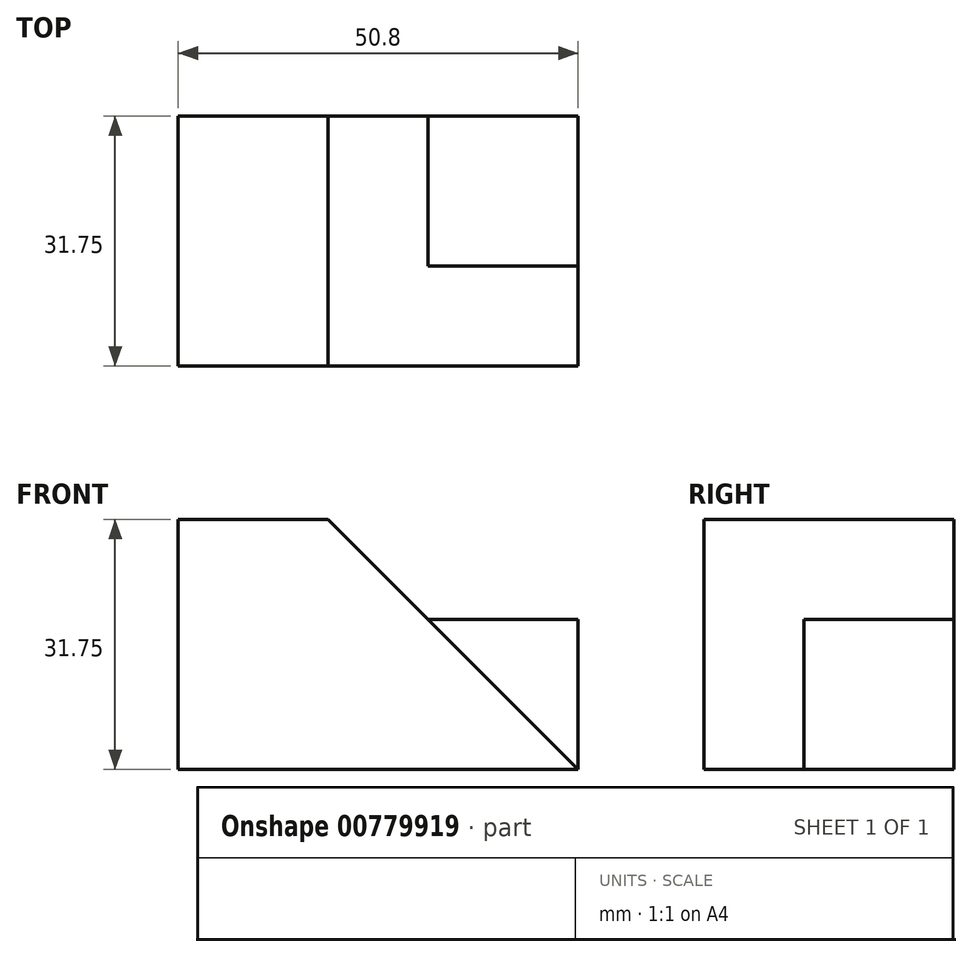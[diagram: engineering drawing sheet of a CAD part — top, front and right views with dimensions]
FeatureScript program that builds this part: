
annotation { "Feature Type Name" : "Feature", "Feature Type Description" : "" }
export const myFeature = defineFeature(function(context is Context, id is Id, definition is map)
    precondition{}
    {
        {
            var Q0;
            Q0=qCreatedBy(makeId("Front.planeOp"),FACE);
            var sketch = newSketch(context, id + "F0", { "sketchPlane" : qUnion([Q0])});
            skLineSegment(sketch, "E0", {"start": v(0, 0) * mm, "end": v(0, 31.75) * mm});
            skLineSegment(sketch, "E1", {"start": v(0, 31.75) * mm, "end": v(19.05, 31.75) * mm});
            skLineSegment(sketch, "E2", {"start": v(0, 0) * mm, "end": v(50.8, 0) * mm});
            skLineSegment(sketch, "E3", {"start": v(50.8, 0) * mm, "end": v(19.05, 31.75) * mm});
            skLineSegment(sketch, "E4", {"start": v(50.8, 0) * mm, "end": v(50.8, 19.05) * mm});
            skLineSegment(sketch, "E5", {"start": v(50.8, 19.05) * mm, "end": v(31.75, 19.05) * mm});
            skSolve(sketch);
        }
        {
            var Q0;
            Q0 = qSketchRegion(id + "F0", true);
            extrude(context, id + "F1", {"entities" : qUnion([Q0]), "depth" : 31.75 * mm, "offsetDistance" : 25.4 * mm});
        }
        {
            var Q0;
            Q0=makeQuery(id+"F1.opExtrude","CAP_FACE",FACE,{"disambiguationData":[OSD([sQuery(id+"F0.wireOp",EDGE,"E0"),sQuery(id+"F0.wireOp",EDGE,"E1"),sQuery(id+"F0.wireOp",EDGE,"E2"),sQuery(id+"F0.wireOp",EDGE,"E3"),sQuery(id+"F0.wireOp",EDGE,"E4"),sQuery(id+"F0.wireOp",EDGE,"E5")])],"isStart":false});
            var sketch = newSketch(context, id + "F2", { "sketchPlane" : qUnion([Q0])});
            skLineSegment(sketch, "E6", {"start": v(31.75, 19.05) * mm, "end": v(50.8, 0) * mm});
            skSolve(sketch);
        }
        {
            var Q0;
            Q0=makeQuery(id+"F2.imprint","IMPRINT",FACE,{"disambiguationData":[TD([[makeQuery(id+"F2.imprint","IMPRINT",EDGE,{"derivedFrom":sQuery(id+"F2.wireOp",EDGE,"E6")}),1.0]])]});
            extrude(context, id + "F3", {"entities" : qUnion([Q0]), "operationType" : NewBodyOperationType.REMOVE, "oppositeDirection" : true, "depth" : 12.7 * mm, "offsetDistance" : 25.4 * mm});
        }
    });
